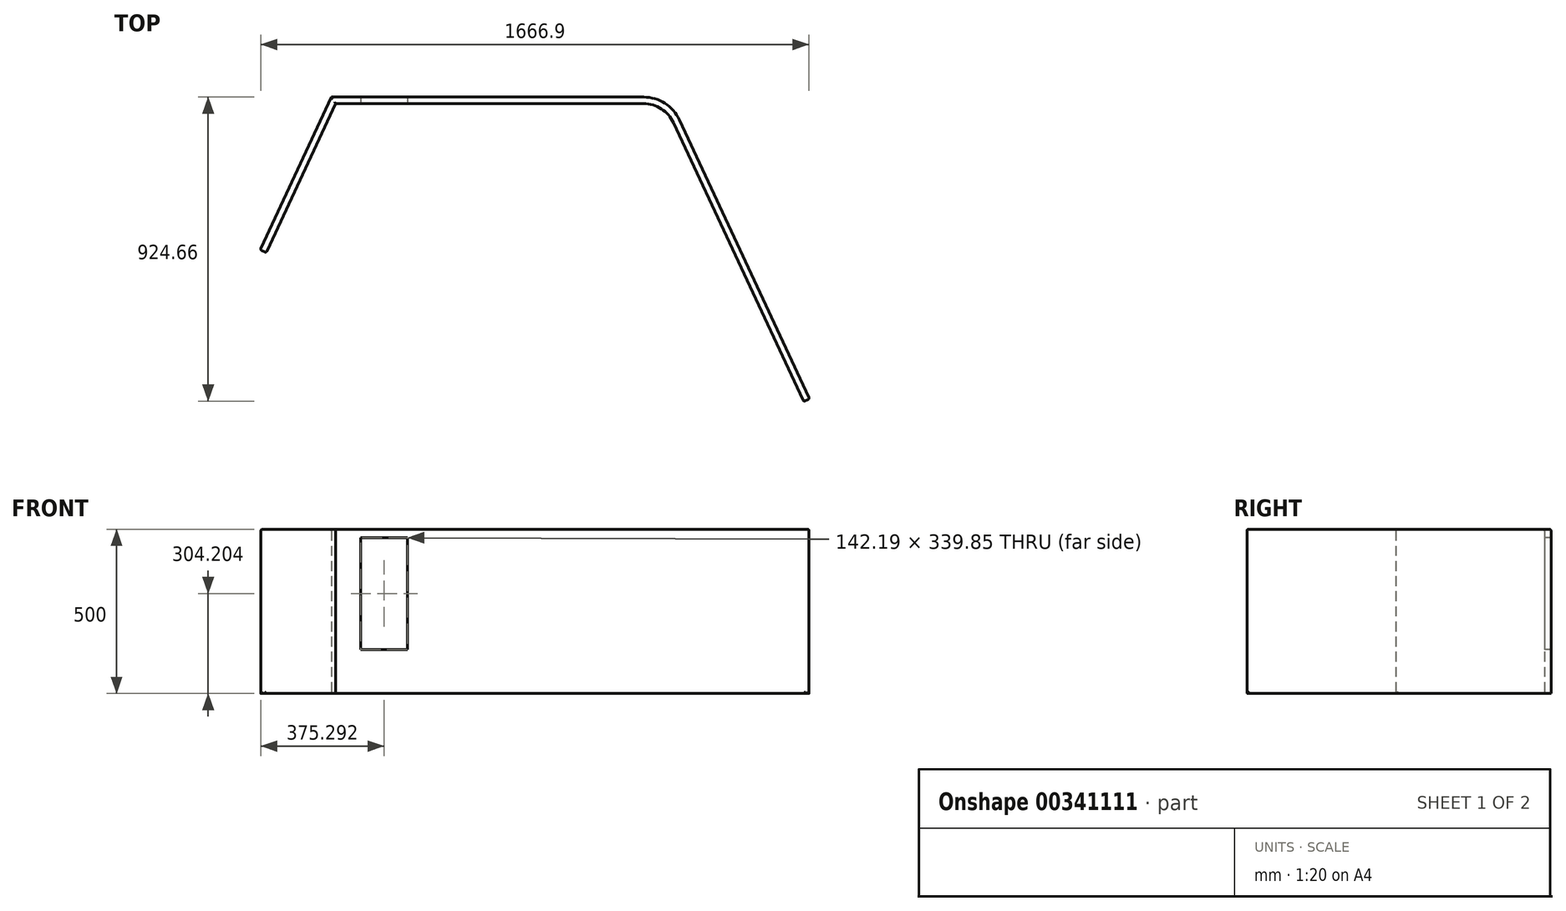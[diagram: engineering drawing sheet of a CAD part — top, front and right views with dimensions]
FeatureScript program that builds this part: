
annotation { "Feature Type Name" : "Feature", "Feature Type Description" : "" }
export const myFeature = defineFeature(function(context is Context, id is Id, definition is map)
    precondition{}
    {
        {
            var Q0;
            Q0=qCreatedBy(makeId("Top.planeOp"),FACE);
            var sketch = newSketch(context, id + "F0", { "sketchPlane" : qUnion([Q0])});
            skLineSegment(sketch, "E0", {"start": v(-676.28, -170.34) * mm, "end": v(-464.97, 282.82) * mm});
            skLineSegment(sketch, "E1", {"start": v(-464.97, 282.82) * mm, "end": v(471.32, 282.82) * mm});
            skLineSegment(sketch, "E2", {"start": v(561.95, 225.08) * mm, "end": v(957.64, -623.49) * mm});
            skLineSegment(sketch, "E3.0", {"start": v(580.08, 233.53) * mm, "end": v(975.77, -615.04) * mm});
            skLineSegment(sketch, "E3.1", {"start": v(-477.72, 302.82) * mm, "end": v(471.32, 302.82) * mm});
            skLineSegment(sketch, "E3.2", {"start": v(-694.4, -161.88) * mm, "end": v(-477.72, 302.82) * mm});
            skLineSegment(sketch, "E4", {"start": v(-694.4, -161.88) * mm, "end": v(-676.28, -170.34) * mm});
            skLineSegment(sketch, "E5", {"start": v(957.64, -623.49) * mm, "end": v(975.77, -615.04) * mm});
            skPoint(sketch, "E6.visualSharp", {"position": v(535.03, 282.82) * mm});
            skArc(sketch, "E6.filletArc", {"start": v(561.95, 225.08) * mm, "mid": v(525.05, 267.16) * mm, "end": v(471.32, 282.82) * mm});
            skPoint(sketch, "E7.visualSharp", {"position": v(547.77, 302.82) * mm});
            skArc(sketch, "E7.filletArc", {"start": v(580.08, 233.53) * mm, "mid": v(535.8, 284.03) * mm, "end": v(471.32, 302.82) * mm});
            skSolve(sketch);
        }
        {
            var Q0;
            Q0=makeQuery(id+"F0.imprint","IMPRINT",FACE,{"disambiguationData":[TD([[makeQuery(id+"F0.imprint","IMPRINT",EDGE,{"derivedFrom":sQuery(id+"F0.wireOp",EDGE,"E0")}),1.0]])]});
            extrude(context, id + "F1", {"entities" : qUnion([Q0]), "depth" : 500 * mm});
        }
        {
            var Q0;
            Q0=makeQuery(id+"F1.opExtrude","SWEPT_FACE",FACE,{"disambiguationData":[OSD([sQuery(id+"F0.wireOp",EDGE,"E1")])]});
            var sketch = newSketch(context, id + "F2", { "sketchPlane" : qUnion([Q0])});
            skLineSegment(sketch, "E8.bottom", {"start": v(-388.57, 474.13) * mm, "end": v(-246.39, 474.13) * mm});
            skLineSegment(sketch, "E8.top", {"start": v(-388.57, 134.28) * mm, "end": v(-246.39, 134.28) * mm});
            skLineSegment(sketch, "E8.left", {"start": v(-388.57, 474.13) * mm, "end": v(-388.57, 134.28) * mm});
            skLineSegment(sketch, "E8.right", {"start": v(-246.39, 474.13) * mm, "end": v(-246.39, 134.28) * mm});
            skSolve(sketch);
        }
        {
            var Q0;
            Q0=makeQuery(id+"F2.imprint","IMPRINT",FACE,{"disambiguationData":[TD([[makeQuery(id+"F2.imprint","IMPRINT",EDGE,{"derivedFrom":sQuery(id+"F2.wireOp",EDGE,"E8.bottom")}),-1.0]])]});
            extrude(context, id + "F3", {"entities" : qUnion([Q0]), "operationType" : NewBodyOperationType.REMOVE, "oppositeDirection" : true, "depth" : 33 * mm});
        }
        {
            var Q0;
            Q0=makeQuery(id+"F1.opExtrude","CAP_FACE",FACE,{"disambiguationData":[OSD([sQuery(id+"F0.wireOp",EDGE,"E0"),sQuery(id+"F0.wireOp",EDGE,"E1"),sQuery(id+"F0.wireOp",EDGE,"E2"),sQuery(id+"F0.wireOp",EDGE,"E3.0"),sQuery(id+"F0.wireOp",EDGE,"E3.1"),sQuery(id+"F0.wireOp",EDGE,"E3.2"),sQuery(id+"F0.wireOp",EDGE,"E4"),sQuery(id+"F0.wireOp",EDGE,"E5"),sQuery(id+"F0.wireOp",EDGE,"E6.filletArc"),sQuery(id+"F0.wireOp",EDGE,"E7.filletArc")])],"isStart":false});
            var Q1;
            Q1=makeQuery(id+"F1.opExtrude","SWEPT_FACE",FACE,{"disambiguationData":[OSD([sQuery(id+"F0.wireOp",EDGE,"E4")])]});
            var Q2;
            Q2=makeQuery(id+"F1.opExtrude","SWEPT_FACE",FACE,{"disambiguationData":[OSD([sQuery(id+"F0.wireOp",EDGE,"E5")])]});
            fillet(context, id + "F4", {"entities" : qUnion([Q0, Q1, Q2]), "radius" : 5 * mm, "tangentPropagation" : true, "allowEdgeOverflow" : false});
        }
    });
